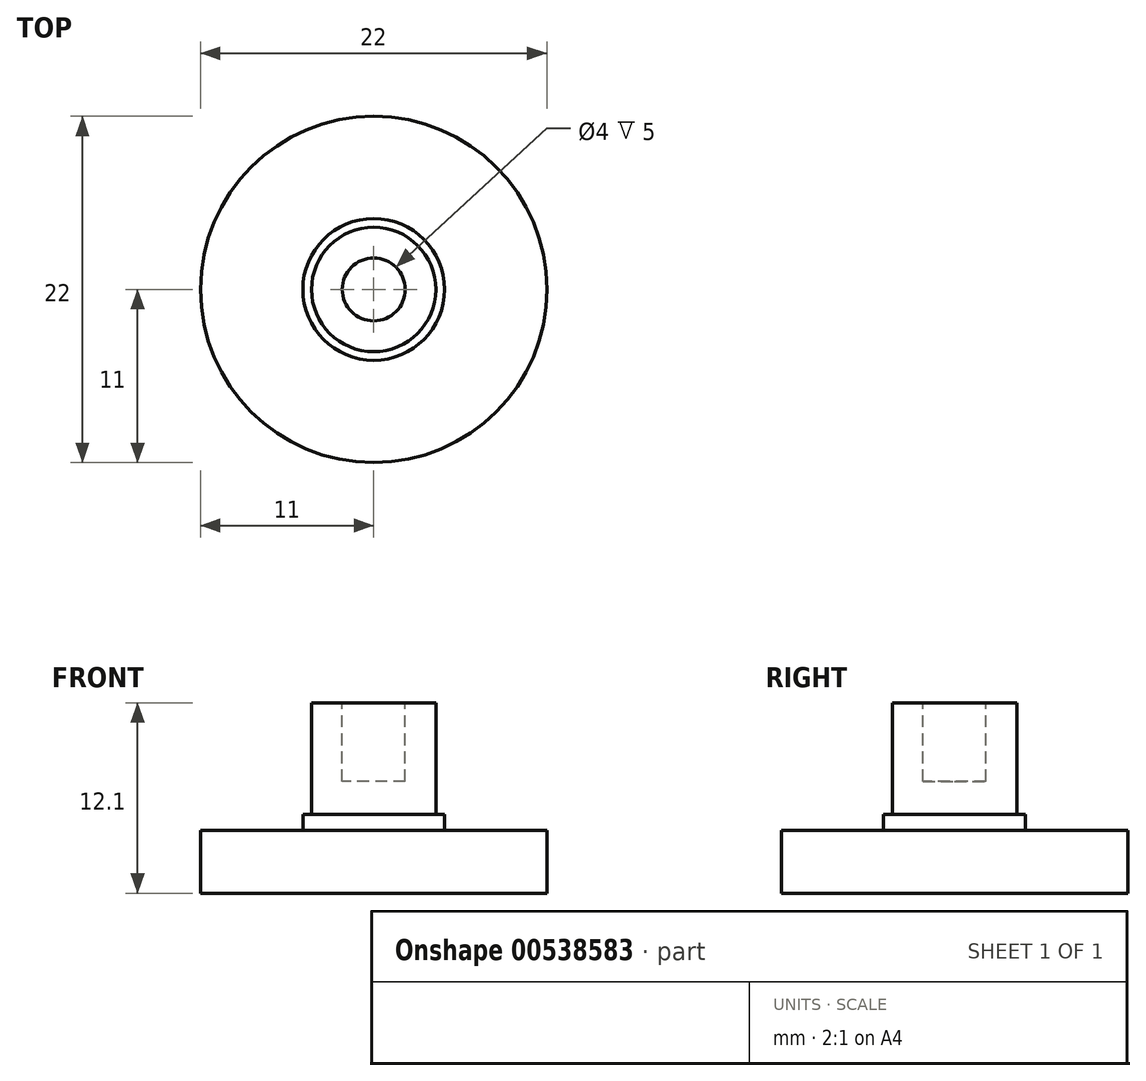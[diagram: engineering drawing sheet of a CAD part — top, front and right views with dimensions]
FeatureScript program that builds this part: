
annotation { "Feature Type Name" : "Feature", "Feature Type Description" : "" }
export const myFeature = defineFeature(function(context is Context, id is Id, definition is map)
    precondition{}
    {
        {
            var Q0;
            Q0=qCreatedBy(makeId("Top.planeOp"),FACE);
            var sketch = newSketch(context, id + "F0", { "sketchPlane" : qUnion([Q0])});
            skCircle(sketch, "E0", {"center": v(0, 0) * mm, "radius": 11 * mm});
            skSolve(sketch);
        }
        {
            var Q0;
            Q0=makeQuery(id+"F0.imprint","IMPRINT",FACE,{"disambiguationData":[TD([[makeQuery(id+"F0.imprint","IMPRINT",EDGE,{"derivedFrom":sQuery(id+"F0.wireOp",EDGE,"E0")}),1.0]])]});
            extrude(context, id + "F1", {"entities" : qUnion([Q0]), "depth" : 4 * mm, "offsetDistance" : 25 * mm});
        }
        {
            var Q0;
            Q0=makeQuery(id+"F1.opExtrude","CAP_FACE",FACE,{"disambiguationData":[OSD([sQuery(id+"F0.wireOp",EDGE,"E0")])],"isStart":false});
            var sketch = newSketch(context, id + "F2", { "sketchPlane" : qUnion([Q0])});
            skCircle(sketch, "E1", {"center": v(0, 0) * mm, "radius": 4.5 * mm});
            skSolve(sketch);
        }
        {
            var Q0;
            Q0=makeQuery(id+"F2.imprint","IMPRINT",FACE,{"disambiguationData":[TD([[makeQuery(id+"F2.imprint","IMPRINT",EDGE,{"derivedFrom":sQuery(id+"F2.wireOp",EDGE,"E1")}),1.0]])]});
            extrude(context, id + "F3", {"entities" : qUnion([Q0]), "operationType" : NewBodyOperationType.ADD, "depth" : 1 * mm, "offsetDistance" : 25 * mm});
        }
        {
            var Q0;
            Q0=makeQuery(id+"F3.opExtrude","CAP_FACE",FACE,{"disambiguationData":[OSD([sQuery(id+"F2.wireOp",EDGE,"E1")])],"isStart":false});
            var sketch = newSketch(context, id + "F4", { "sketchPlane" : qUnion([Q0])});
            skCircle(sketch, "E2", {"center": v(0, 0) * mm, "radius": 3.95 * mm});
            skSolve(sketch);
        }
        {
            var Q0;
            Q0=makeQuery(id+"F4.imprint","IMPRINT",FACE,{"disambiguationData":[TD([[makeQuery(id+"F4.imprint","IMPRINT",EDGE,{"derivedFrom":sQuery(id+"F4.wireOp",EDGE,"E2")}),1.0]])]});
            extrude(context, id + "F5", {"entities" : qUnion([Q0]), "operationType" : NewBodyOperationType.ADD, "depth" : 7.1 * mm, "offsetDistance" : 25 * mm});
        }
        {
            var Q0;
            Q0=makeQuery(id+"F5.opExtrude","CAP_FACE",FACE,{"disambiguationData":[OSD([sQuery(id+"F4.wireOp",EDGE,"E2")])],"isStart":false});
            var sketch = newSketch(context, id + "F6", { "sketchPlane" : qUnion([Q0])});
            skCircle(sketch, "E3", {"center": v(0, 0) * mm, "radius": 2 * mm});
            skSolve(sketch);
        }
        {
            var Q0;
            Q0=makeQuery(id+"F6.imprint","IMPRINT",FACE,{"disambiguationData":[TD([[makeQuery(id+"F6.imprint","IMPRINT",EDGE,{"derivedFrom":sQuery(id+"F6.wireOp",EDGE,"E3")}),1.0]])]});
            extrude(context, id + "F7", {"entities" : qUnion([Q0]), "operationType" : NewBodyOperationType.REMOVE, "oppositeDirection" : true, "depth" : 5 * mm, "offsetDistance" : 25 * mm});
        }
    });
